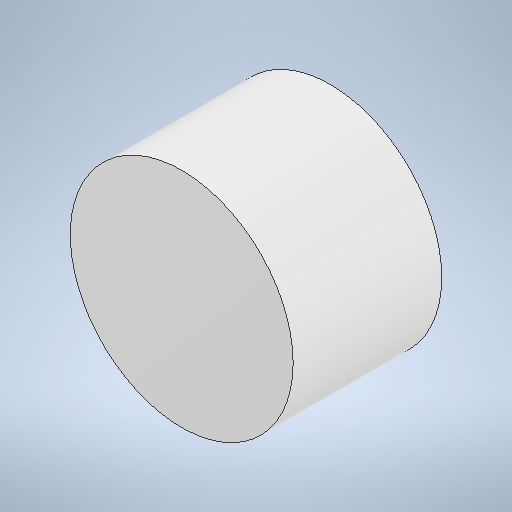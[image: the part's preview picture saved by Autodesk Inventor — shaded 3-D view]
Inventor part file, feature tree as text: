
AUTODESK INVENTOR PART (.ipt)
format: ipt  version: 2025.2 (Build 292293000, 293)  size: 238,592 bytes
history: native  units: mm
features: other x1, extrude x1, sketch x1
ambient origin geometry x8: Origin, YZ Plane, XZ Plane, XY Plane, X Axis, Y Axis, Z Axis, Center Point
bodies: Body1 (feature_tree)
feature tree (3):
  other  "Sólido1"
  extrude  "Extrusão1"  Depth=10.0mm TaperAngle=0.0deg
  sketch  "Esboço1"  dims[d0=15.0mm d1=10.0mm d2=0.0mm]
